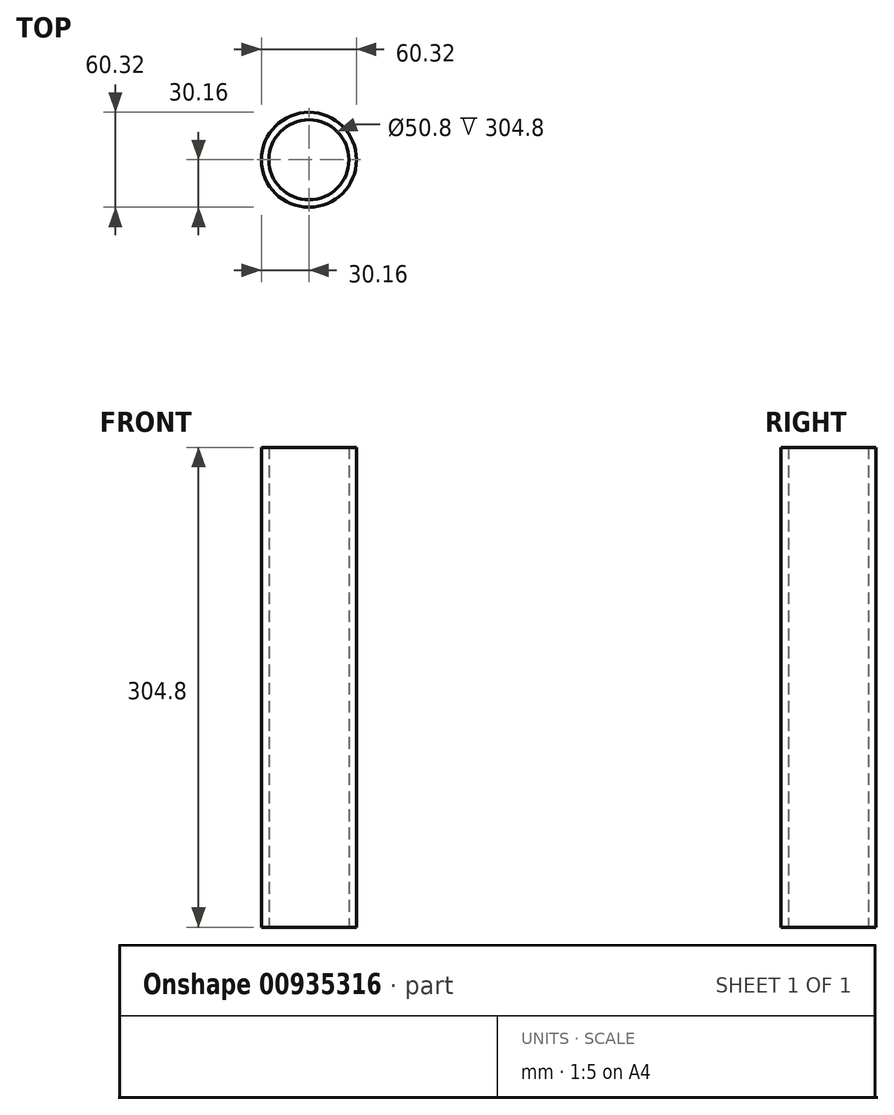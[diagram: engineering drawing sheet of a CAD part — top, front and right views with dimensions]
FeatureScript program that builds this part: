
annotation { "Feature Type Name" : "Feature", "Feature Type Description" : "" }
export const myFeature = defineFeature(function(context is Context, id is Id, definition is map)
    precondition{}
    {
        {
            var Q0;
            Q0=qCreatedBy(makeId("Top.planeOp"),FACE);
            var sketch = newSketch(context, id + "F0", { "sketchPlane" : qUnion([Q0])});
            skCircle(sketch, "E0", {"center": v(0, 0) * mm, "radius": 25.4 * mm});
            skCircle(sketch, "E1", {"center": v(0, 0) * mm, "radius": 30.16 * mm});
            skSolve(sketch);
        }
        {
            var Q0;
            Q0=makeQuery(id+"F0.imprint","IMPRINT",FACE,{"disambiguationData":[TD([[makeQuery(id+"F0.imprint","IMPRINT",EDGE,{"derivedFrom":sQuery(id+"F0.wireOp",EDGE,"E0")}),-1.0]])]});
            extrude(context, id + "F1", {"entities" : qUnion([Q0]), "offsetDistance" : 25 * mm, "depth" : 304.8 * mm});
        }
    });
